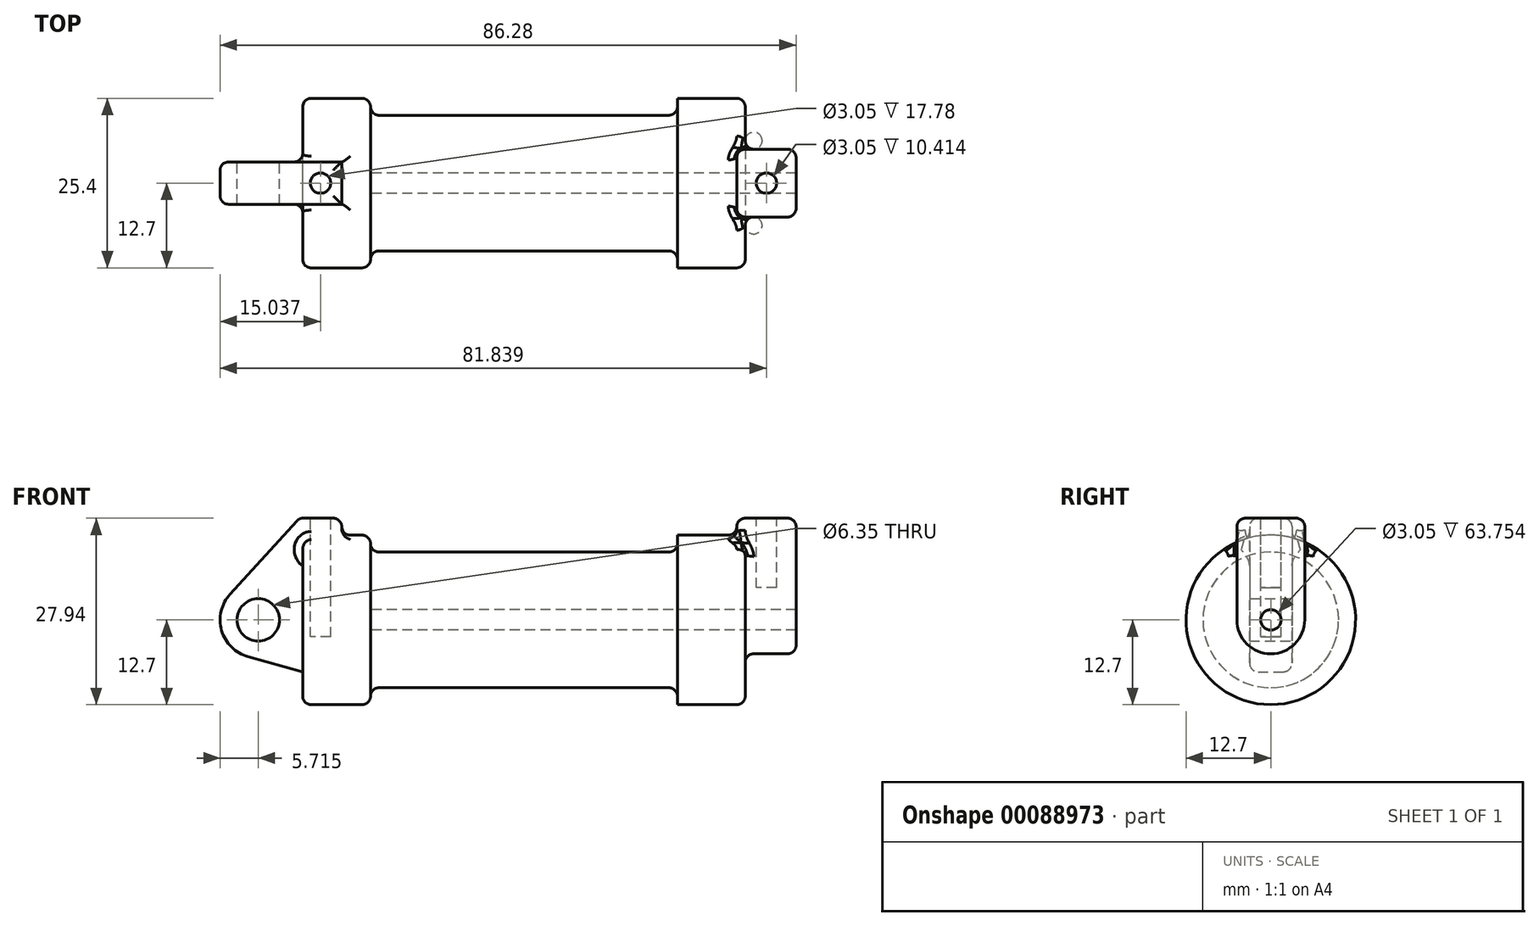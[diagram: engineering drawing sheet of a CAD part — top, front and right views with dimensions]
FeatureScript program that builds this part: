
annotation { "Feature Type Name" : "Feature", "Feature Type Description" : "" }
export const myFeature = defineFeature(function(context is Context, id is Id, definition is map)
    precondition{}
    {
        {
            var Q0;
            Q0=qCreatedBy(makeId("Front.planeOp"),FACE);
            var sketch = newSketch(context, id + "F0", { "sketchPlane" : qUnion([Q0])});
            skLineSegment(sketch, "E0", {"start": v(0, 0) * mm, "end": v(0, 12.7) * mm});
            skLineSegment(sketch, "E1", {"start": v(0, 12.7) * mm, "end": v(10.16, 12.7) * mm});
            skLineSegment(sketch, "E2", {"start": v(10.16, 12.7) * mm, "end": v(10.16, 10.16) * mm});
            skLineSegment(sketch, "E3", {"start": v(10.16, 10.16) * mm, "end": v(56.13, 10.16) * mm});
            skLineSegment(sketch, "E4", {"start": v(56.13, 10.16) * mm, "end": v(56.13, 12.7) * mm});
            skLineSegment(sketch, "E5", {"start": v(56.13, 12.7) * mm, "end": v(66.3, 12.7) * mm});
            skLineSegment(sketch, "E6", {"start": v(66.3, 12.7) * mm, "end": v(66.3, 0) * mm});
            skLineSegment(sketch, "E7", {"start": v(66.3, 0) * mm, "end": v(0, 0) * mm});
            skLineSegment(sketch, "E8", {"start": v(5.84, 15.24) * mm, "end": v(-0.5, 15.24) * mm});
            skLineSegment(sketch, "E9", {"start": v(-0.5, 15.24) * mm, "end": v(-10.88, 3.85) * mm});
            skLineSegment(sketch, "E10", {"start": v(0, 0) * mm, "end": v(-6.65, 0) * mm});
            skCircle(sketch, "E11", {"center": v(-6.65, 0) * mm, "radius": 5.72 * mm});
            skCircle(sketch, "E12", {"center": v(-6.65, 0) * mm, "radius": 3.18 * mm});
            skLineSegment(sketch, "E13", {"start": v(5.84, 15.24) * mm, "end": v(5.84, -9.4) * mm});
            skLineSegment(sketch, "E14", {"start": v(5.84, -9.4) * mm, "end": v(-8.18, -5.5) * mm});
            skSolve(sketch);
        }
        {
            var Q0;
            {var subQ0=sQuery(id+"F0.wireOp",EDGE,"E0");Q0=makeQuery(id+"F0.imprint","IMPRINT",FACE,{"disambiguationData":[TD([[makeQuery(id+"F0.imprint","IMPRINT",EDGE,{"derivedFrom":subQ0}),-1.0]])]});}
            var Q1;
            {var subQ0=sQuery(id+"F0.wireOp",EDGE,"E2");Q1=makeQuery(id+"F0.imprint","IMPRINT",FACE,{"disambiguationData":[TD([[makeQuery(id+"F0.imprint","IMPRINT",EDGE,{"derivedFrom":subQ0}),-1.0]])]});}
            var Q2;
            Q2=sQuery(id+"F0.wireOp",EDGE,"E7");
            revolve(context, id + "F1", {"entities" : qUnion([Q0, Q1]), "axis" : qUnion([Q2]), "revolveType" : RevolveType.FULL});
        }
        {
            var Q0;
            {var subQ3=sQuery(id+"F0.wireOp",EDGE,"E0");Q0=makeQuery(id+"F0.imprint","IMPRINT",FACE,{"disambiguationData":[TD([[makeQuery(id+"F0.imprint","IMPRINT",EDGE,{"derivedFrom":subQ3}),1.0]])]});}
            var Q1;
            {var subQ4=sQuery(id+"F0.wireOp",EDGE,"E12");Q1=makeQuery(id+"F0.imprint","IMPRINT",FACE,{"disambiguationData":[TD([[makeQuery(id+"F0.imprint","IMPRINT",EDGE,{"derivedFrom":subQ4}),-1.0]])]});}
            var Q2;
            {var subQ0=sQuery(id+"F0.wireOp",EDGE,"E14");Q2=makeQuery(id+"F0.imprint","IMPRINT",FACE,{"disambiguationData":[TD([[makeQuery(id+"F0.imprint","IMPRINT",EDGE,{"derivedFrom":subQ0}),-1.0]])]});}
            var Q3;
            {var subQ0=sQuery(id+"F0.wireOp",EDGE,"E0");Q3=makeQuery(id+"F0.imprint","IMPRINT",FACE,{"disambiguationData":[TD([[makeQuery(id+"F0.imprint","IMPRINT",EDGE,{"derivedFrom":subQ0}),-1.0]])]});}
            extrude(context, id + "F2", {"entities" : qUnion([Q0, Q1, Q2, Q3]), "operationType" : NewBodyOperationType.ADD, "endBound" : BoundingType.SYMMETRIC, "depth" : 6.35 * mm});
        }
        {
            var Q0;
            Q0=makeQuery(id+"F1.opRevolve","SWEPT_FACE",FACE,{"disambiguationData":[OSD([sQuery(id+"F0.wireOp",EDGE,"E6")])]});
            var sketch = newSketch(context, id + "F3", { "sketchPlane" : qUnion([Q0])});
            skCircle(sketch, "E15", {"center": v(0, 0) * mm, "radius": 5.08 * mm});
            skCircle(sketch, "E16", {"center": v(0, 0) * mm, "radius": 1.52 * mm});
            skLineSegment(sketch, "E17", {"start": v(-5.08, 0) * mm, "end": v(-5.08, 15.24) * mm});
            skLineSegment(sketch, "E18", {"start": v(5.08, 0) * mm, "end": v(5.08, 15.24) * mm});
            skLineSegment(sketch, "E19", {"start": v(5.08, 15.24) * mm, "end": v(-5.08, 15.24) * mm});
            skSolve(sketch);
        }
        {
            var Q0;
            Q0=makeQuery(id+"F3.imprint","IMPRINT",FACE,{"disambiguationData":[TD([[makeQuery(id+"F3.imprint","IMPRINT",EDGE,{"derivedFrom":sQuery(id+"F3.wireOp",EDGE,"E16")}),-1.0]])]});
            var Q1;
            {var subQ0=sQuery(id+"F3.wireOp",EDGE,"E17");var subQ1=sQuery(id+"F3.wireOp",EDGE,"E15");var subQ2=makeQuery(id+"F3.imprint","INTERSECT",VERTEX,{"derivedFrom":[subQ1,subQ0]});Q1=makeQuery(id+"F3.imprint","IMPRINT",FACE,{"disambiguationData":[TD([[makeQuery(id+"F3.imprint","IMPRINT",EDGE,{"disambiguationData":[TD([[subQ2,1.0]])],"derivedFrom":subQ1}),-1.0]])]});}
            var Q2;
            {var subQ0=sQuery(id+"F3.wireOp",EDGE,"E19");Q2=makeQuery(id+"F3.imprint","IMPRINT",FACE,{"disambiguationData":[TD([[makeQuery(id+"F3.imprint","IMPRINT",EDGE,{"derivedFrom":subQ0}),1.0]])]});}
            extrude(context, id + "F4", {"entities" : qUnion([Q0, Q1, Q2]), "operationType" : NewBodyOperationType.ADD, "depth" : 7.62 * mm});
        }
        {
            var Q0;
            Q0=makeQuery(id+"F4.opExtrude","CAP_FACE",FACE,{"disambiguationData":[OSD([sQuery(id+"F3.wireOp",EDGE,"E15"),sQuery(id+"F3.wireOp",EDGE,"E16"),sQuery(id+"F3.wireOp",EDGE,"E17"),sQuery(id+"F3.wireOp",EDGE,"E18"),sQuery(id+"F3.wireOp",EDGE,"E19")])],"isStart":true});
            extrude(context, id + "F5", {"entities" : qUnion([Q0]), "operationType" : NewBodyOperationType.ADD, "depth" : 1.27 * mm});
        }
        {
            var Q0;
            Q0=makeQuery(id+"F4.boolean.opBoolean","SPLIT",FACE,{"disambiguationData":[TD([makeQuery(id+"F4.opExtrude","SWEPT_FACE",FACE,{"disambiguationData":[OSD([sQuery(id+"F3.wireOp",EDGE,"E16")])]})])],"derivedFrom":makeQuery(id+"F1.opRevolve","SWEPT_FACE",FACE,{"disambiguationData":[OSD([sQuery(id+"F0.wireOp",EDGE,"E6")])]})});
            var Q1;
            Q1=makeQuery(id+"F1.opRevolve","SWEPT_FACE",FACE,{"disambiguationData":[OSD([sQuery(id+"F0.wireOp",EDGE,"E2")])]});
            extrude(context, id + "F6", {"entities" : qUnion([Q0]), "operationType" : NewBodyOperationType.REMOVE, "endBound" : BoundingType.UP_TO_SURFACE, "oppositeDirection" : true, "endBoundEntityFace" : qUnion([Q1]), "depth" : 25.4 * mm});
        }
        {
            var Q0;
            Q0=makeQuery(id+"F2.opExtrude","SWEPT_FACE",FACE,{"disambiguationData":[OSD([sQuery(id+"F0.wireOp",EDGE,"E8")])]});
            var sketch = newSketch(context, id + "F7", { "sketchPlane" : qUnion([Q0])});
            skLineSegment(sketch, "E20.0.0", {"start": v(5.84, 3.18) * mm, "end": v(-0.5, 3.18) * mm});
            skLineSegment(sketch, "E20.0.1", {"start": v(-0.5, 3.17) * mm, "end": v(-0.5, -3.18) * mm});
            skLineSegment(sketch, "E20.0.2", {"start": v(-0.5, -3.18) * mm, "end": v(5.84, -3.18) * mm});
            skLineSegment(sketch, "E20.0.3", {"start": v(5.84, -3.18) * mm, "end": v(5.84, 3.17) * mm});
            skCircle(sketch, "E21", {"center": v(2.67, 0) * mm, "radius": 1.52 * mm});
            skLineSegment(sketch, "E22.0.0", {"start": v(73.91, 5.08) * mm, "end": v(65.02, 5.08) * mm});
            skLineSegment(sketch, "E22.0.1", {"start": v(65.02, 5.08) * mm, "end": v(65.02, -5.08) * mm});
            skLineSegment(sketch, "E22.0.2", {"start": v(65.02, -5.08) * mm, "end": v(73.91, -5.08) * mm});
            skLineSegment(sketch, "E22.0.3", {"start": v(73.91, -5.08) * mm, "end": v(73.91, 5.08) * mm});
            skCircle(sketch, "E23", {"center": v(69.47, 0) * mm, "radius": 1.52 * mm});
            skSolve(sketch);
        }
        {
            var Q0;
            Q0=makeQuery(id+"F7.imprint","IMPRINT",FACE,{"disambiguationData":[TD([[makeQuery(id+"F7.imprint","IMPRINT",EDGE,{"derivedFrom":sQuery(id+"F7.wireOp",EDGE,"E21")}),1.0]])]});
            extrude(context, id + "F8", {"entities" : qUnion([Q0]), "operationType" : NewBodyOperationType.REMOVE, "oppositeDirection" : true, "depth" : 17.78 * mm});
        }
        {
            var Q0;
            Q0=makeQuery(id+"F7.imprint","IMPRINT",FACE,{"disambiguationData":[TD([[makeQuery(id+"F7.imprint","IMPRINT",EDGE,{"derivedFrom":sQuery(id+"F7.wireOp",EDGE,"E23")}),1.0]])]});
            extrude(context, id + "F9", {"entities" : qUnion([Q0]), "operationType" : NewBodyOperationType.REMOVE, "oppositeDirection" : true, "depth" : 10.4 * mm});
        }
        {
            var Q0;
            Q0=makeQuery(id+"F1.opRevolve","SWEPT_FACE",FACE,{"disambiguationData":[OSD([sQuery(id+"F0.wireOp",EDGE,"E1")])]});
            var Q1;
            Q1=makeQuery(id+"F1.opRevolve","SWEPT_FACE",FACE,{"disambiguationData":[OSD([sQuery(id+"F0.wireOp",EDGE,"E3")])]});
            var Q2;
            Q2=makeQuery(id+"F4.boolean.opBoolean","SPLIT",FACE,{"disambiguationData":[TD([makeQuery(id+"F1.opRevolve","SWEPT_FACE",FACE,{"disambiguationData":[OSD([sQuery(id+"F0.wireOp",EDGE,"E5")])]})])],"derivedFrom":makeQuery(id+"F1.opRevolve","SWEPT_FACE",FACE,{"disambiguationData":[OSD([sQuery(id+"F0.wireOp",EDGE,"E6")])]})});
            var Q3;
            Q3=makeQuery(id+"F5.opExtrude","CAP_FACE",FACE,{"disambiguationData":[OSD([sQuery(id+"F3.wireOp",EDGE,"E15"),sQuery(id+"F3.wireOp",EDGE,"E16"),sQuery(id+"F3.wireOp",EDGE,"E17"),sQuery(id+"F3.wireOp",EDGE,"E18"),sQuery(id+"F3.wireOp",EDGE,"E19")])],"isStart":false});
            var Q4;
            {var subQ0=sQuery(id+"F3.wireOp",EDGE,"E18");Q4=makeQuery(id+"F5.boolean.opBoolean","MERGE",FACE,{"derivedFrom":[makeQuery(id+"F4.opExtrude","SWEPT_FACE",FACE,{"disambiguationData":[OSD([subQ0])]}),makeQuery(id+"F5.opExtrude","SWEPT_FACE",FACE,{"disambiguationData":[OSD([subQ0])]})]});}
            var Q5;
            Q5=makeQuery(id+"F2.opExtrude","SWEPT_FACE",FACE,{"disambiguationData":[OSD([sQuery(id+"F0.wireOp",EDGE,"E9")])]});
            var Q6;
            {var subQ0=sQuery(id+"F3.wireOp",EDGE,"E17");Q6=makeQuery(id+"F5.boolean.opBoolean","MERGE",FACE,{"derivedFrom":[makeQuery(id+"F4.opExtrude","SWEPT_FACE",FACE,{"disambiguationData":[OSD([subQ0])]}),makeQuery(id+"F5.opExtrude","SWEPT_FACE",FACE,{"disambiguationData":[OSD([subQ0])]})]});}
            var Q7;
            Q7=makeQuery(id+"F4.opExtrude","CAP_EDGE",EDGE,{"disambiguationData":[OSD([sQuery(id+"F3.wireOp",EDGE,"E19")])],"isStart":false});
            var Q8;
            Q8=makeQuery(id+"F2.opExtrude","CAP_EDGE",EDGE,{"disambiguationData":[OSD([sQuery(id+"F0.wireOp",EDGE,"E8")])],"isStart":false});
            var Q9;
            Q9=makeQuery(id+"F2.opExtrude","CAP_EDGE",EDGE,{"disambiguationData":[OSD([sQuery(id+"F0.wireOp",EDGE,"E8")])],"isStart":true});
            var Q10;
            Q10=makeQuery(id+"F2.opExtrude","SWEPT_EDGE",EDGE,{"disambiguationData":[OSD([sQuery(id+"F0.wireOp",EDGE,"E8"),sQuery(id+"F0.wireOp",EDGE,"E13")])]});
            fillet(context, id + "F10", {"entities" : qUnion([Q0, Q1, Q2, Q3, Q4, Q5, Q6, Q7, Q8, Q9, Q10]), "radius" : 1.27 * mm, "tangentPropagation" : true, "allowEdgeOverflow" : false});
        }
    });
